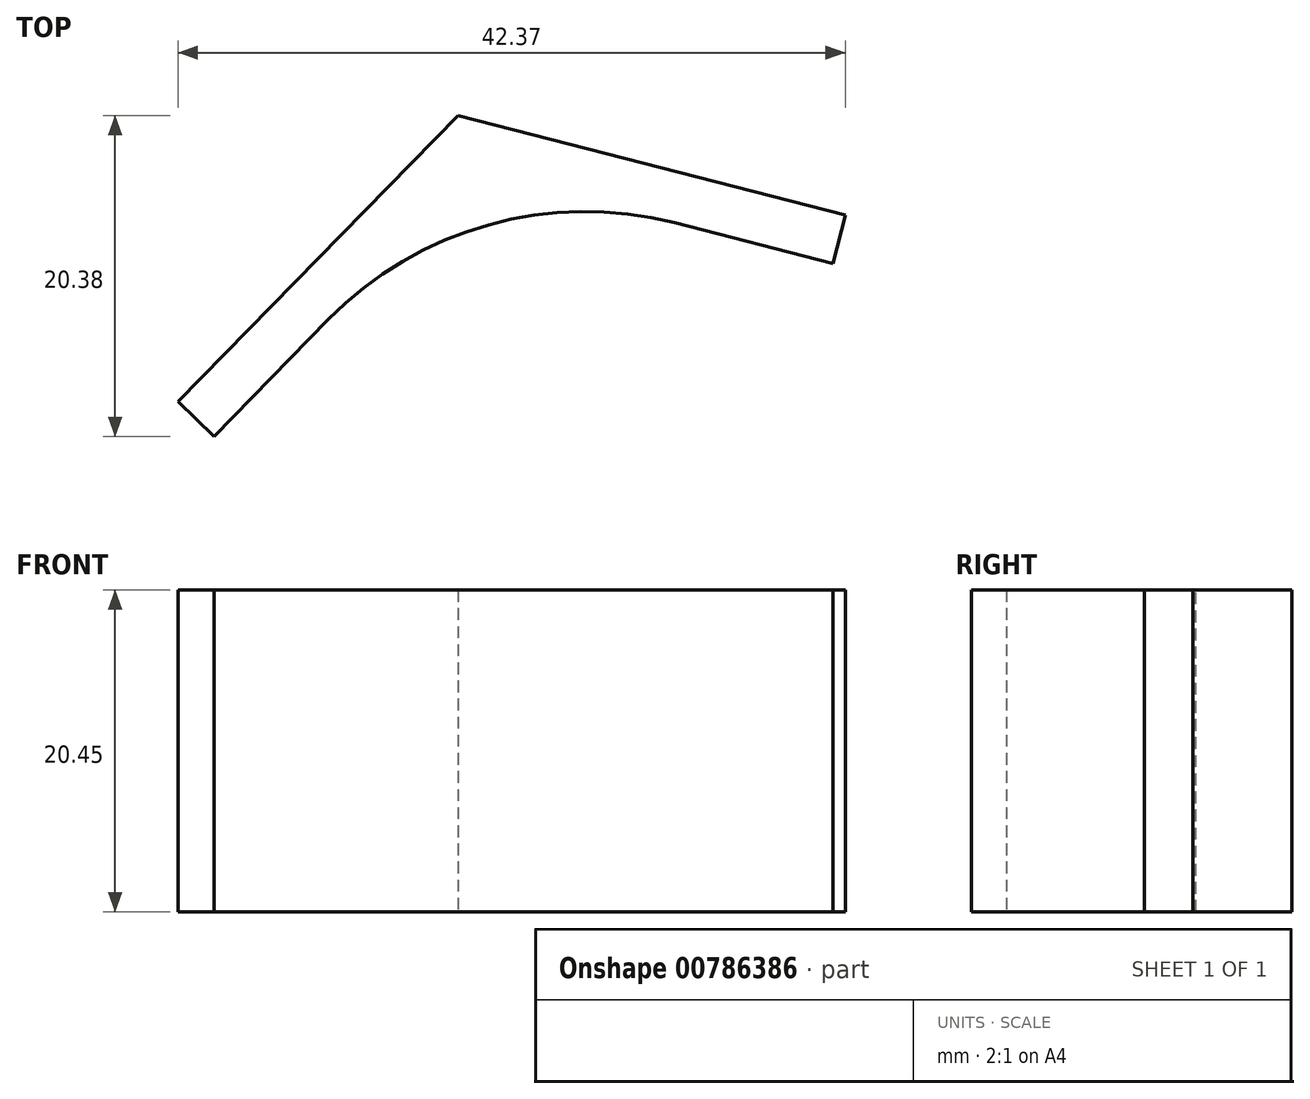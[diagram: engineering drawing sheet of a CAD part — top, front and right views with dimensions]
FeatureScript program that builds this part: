
annotation { "Feature Type Name" : "Feature", "Feature Type Description" : "" }
export const myFeature = defineFeature(function(context is Context, id is Id, definition is map)
    precondition{}
    {
        {
            var Q0;
            Q0=qCreatedBy(makeId("Top.planeOp"),FACE);
            var sketch = newSketch(context, id + "F0", { "sketchPlane" : qUnion([Q0])});
            skLineSegment(sketch, "E0.0", {"start": v(-26.96, 96.38) * mm, "end": v(-2.35, 90.07) * mm});
            skLineSegment(sketch, "E0.5", {"start": v(-44.72, 78.22) * mm, "end": v(-26.96, 96.38) * mm});
            skLineSegment(sketch, "E1", {"start": v(-26.96, 96.38) * mm, "end": v(-44.72, 78.22) * mm});
            skLineSegment(sketch, "E2", {"start": v(-2.35, 90.07) * mm, "end": v(-3.14, 87) * mm});
            skLineSegment(sketch, "E3", {"start": v(-44.72, 78.22) * mm, "end": v(-42.45, 76) * mm});
            skLineSegment(sketch, "E4", {"start": v(-42.45, 76) * mm, "end": v(-25.97, 92.85) * mm});
            skLineSegment(sketch, "E5", {"start": v(-25.97, 92.85) * mm, "end": v(-3.14, 87) * mm});
            skSolve(sketch);
        }
        {
            var Q0;
            Q0 = qSketchRegion(id + "F0", true);
            extrude(context, id + "F1", {"entities" : qUnion([Q0]), "depth" : 20.45 * mm, "offsetDistance" : 25.4 * mm});
        }
        {
            var Q0;
            Q0=makeQuery(id+"F1.opExtrude","SWEPT_EDGE",EDGE,{"disambiguationData":[OSD([sQuery(id+"F0.wireOp",EDGE,"E4"),sQuery(id+"F0.wireOp",EDGE,"E5")])]});
            fillet(context, id + "F2", {"entities" : qUnion([Q0]), "radius" : 22.86 * mm, "tangentPropagation" : true, "allowEdgeOverflow" : false});
        }
    });
